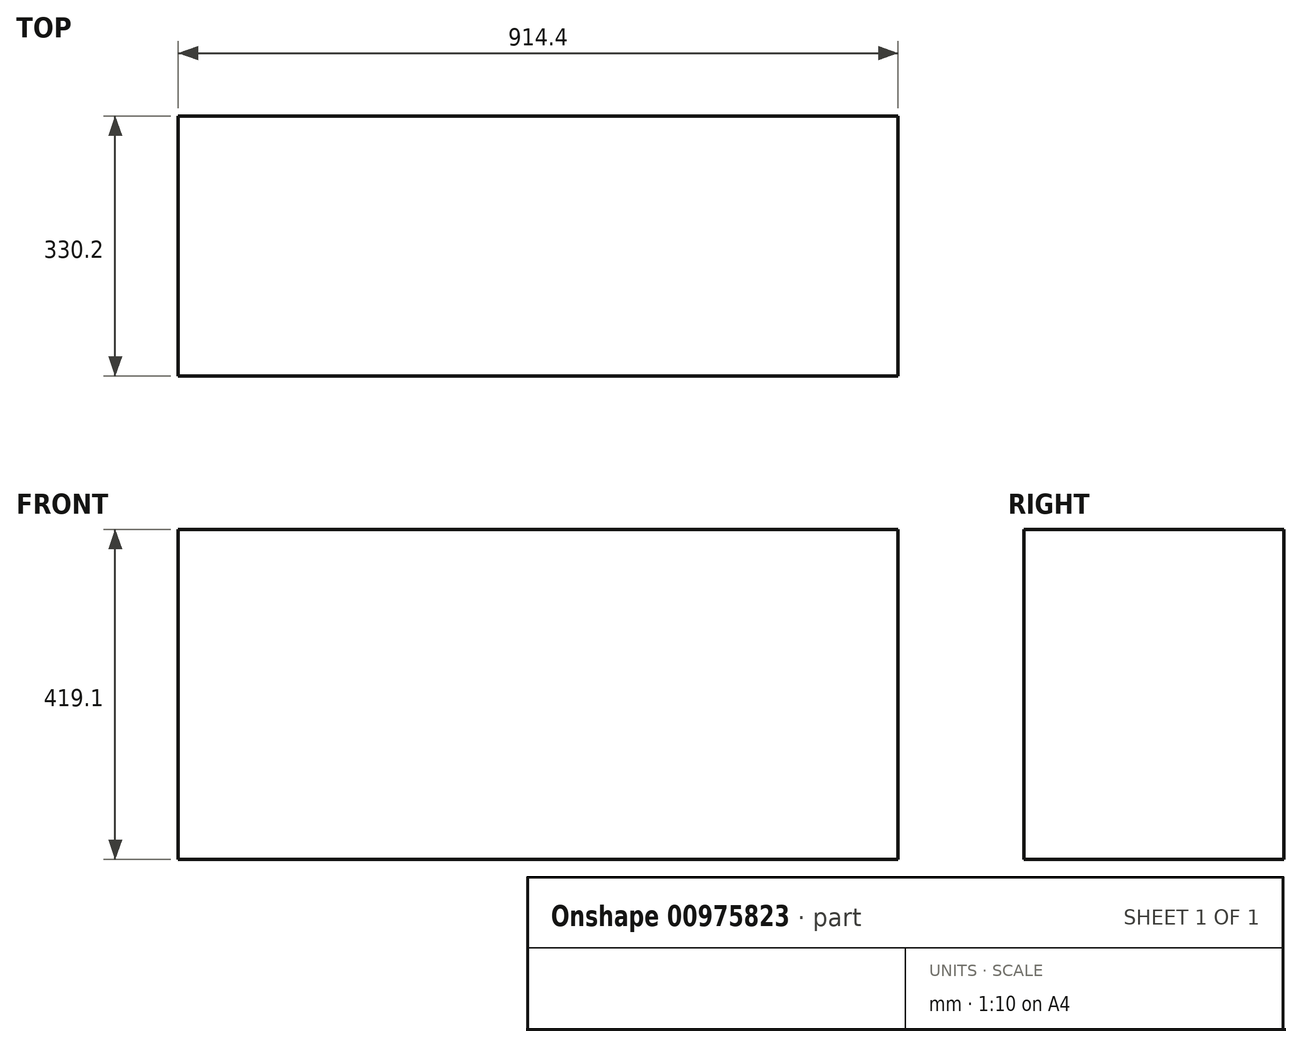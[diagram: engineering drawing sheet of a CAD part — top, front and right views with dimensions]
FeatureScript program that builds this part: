
annotation { "Feature Type Name" : "Feature", "Feature Type Description" : "" }
export const myFeature = defineFeature(function(context is Context, id is Id, definition is map)
    precondition{}
    {
        {
            var Q0;
            Q0=qCreatedBy(makeId("Front.planeOp"),FACE);
            var sketch = newSketch(context, id + "F0", { "sketchPlane" : qUnion([Q0])});
            skLineSegment(sketch, "E0.bottom", {"start": v(457.2, -209.55) * mm, "end": v(-457.2, -209.55) * mm});
            skLineSegment(sketch, "E0.top", {"start": v(457.2, 209.55) * mm, "end": v(-457.2, 209.55) * mm});
            skLineSegment(sketch, "E0.left", {"start": v(457.2, -209.55) * mm, "end": v(457.2, 209.55) * mm});
            skLineSegment(sketch, "E0.right", {"start": v(-457.2, -209.55) * mm, "end": v(-457.2, 209.55) * mm});
            skPoint(sketch, "E0.middle", {"position": v(0, 0) * mm});
            skSolve(sketch);
        }
        {
            var Q0;
            Q0=makeQuery(id+"F0.imprint","IMPRINT",FACE,{"disambiguationData":[TD([[makeQuery(id+"F0.imprint","IMPRINT",EDGE,{"derivedFrom":sQuery(id+"F0.wireOp",EDGE,"E0.bottom")}),-1.0]])]});
            var Q1;
            Q1=sQuery(id+"F0.wireOp",EDGE,"E0.top");
            var Q2;
            Q2=sQuery(id+"F0.wireOp",EDGE,"E0.right");
            extrude(context, id + "F1", {"entities" : qUnion([Q0]), "surfaceEntities" : qUnion([Q1, Q2]), "depth" : 330.2 * mm, "offsetDistance" : 25.4 * mm});
        }
    });
